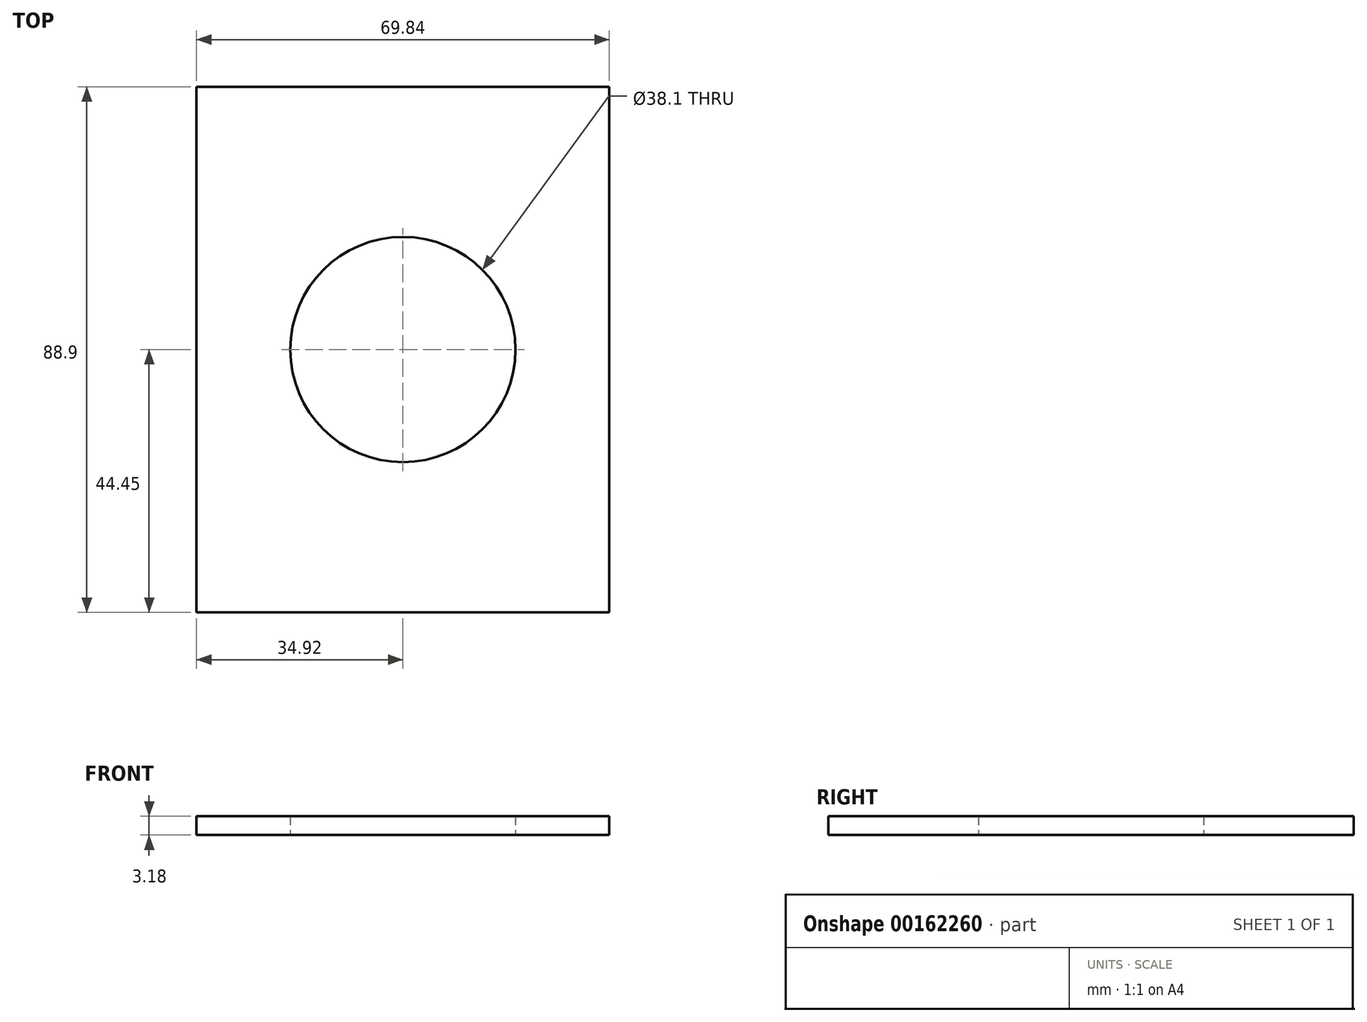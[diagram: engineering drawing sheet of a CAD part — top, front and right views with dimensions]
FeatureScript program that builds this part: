
annotation { "Feature Type Name" : "Feature", "Feature Type Description" : "" }
export const myFeature = defineFeature(function(context is Context, id is Id, definition is map)
    precondition{}
    {
        {
            var Q0;
            Q0=qCreatedBy(makeId("Top.planeOp"),FACE);
            var sketch = newSketch(context, id + "F0", { "sketchPlane" : qUnion([Q0])});
            skLineSegment(sketch, "E0.bottom", {"start": v(34.93, -44.45) * mm, "end": v(-34.93, -44.45) * mm});
            skLineSegment(sketch, "E0.top", {"start": v(34.93, 44.45) * mm, "end": v(-34.93, 44.45) * mm});
            skLineSegment(sketch, "E0.left", {"start": v(34.93, -44.45) * mm, "end": v(34.93, 44.45) * mm});
            skLineSegment(sketch, "E0.right", {"start": v(-34.93, -44.45) * mm, "end": v(-34.93, 44.45) * mm});
            skPoint(sketch, "E0.middle", {"position": v(0, 0) * mm});
            skCircle(sketch, "E1", {"center": v(0, 0) * mm, "radius": 19.05 * mm});
            skCircle(sketch, "E2", {"center": v(0, 0) * mm, "radius": 12.7 * mm});
            skCircle(sketch, "E3", {"center": v(0, 0) * mm, "radius": 7.94 * mm});
            skSolve(sketch);
        }
        {
            var Q0;
            Q0=makeQuery(id+"F0.imprint","IMPRINT",FACE,{"disambiguationData":[TD([[makeQuery(id+"F0.imprint","IMPRINT",EDGE,{"derivedFrom":sQuery(id+"F0.wireOp",EDGE,"E0.bottom")}),-1.0]])]});
            extrude(context, id + "F1", {"entities" : qUnion([Q0]), "depth" : 3.17 * mm});
        }
    });
